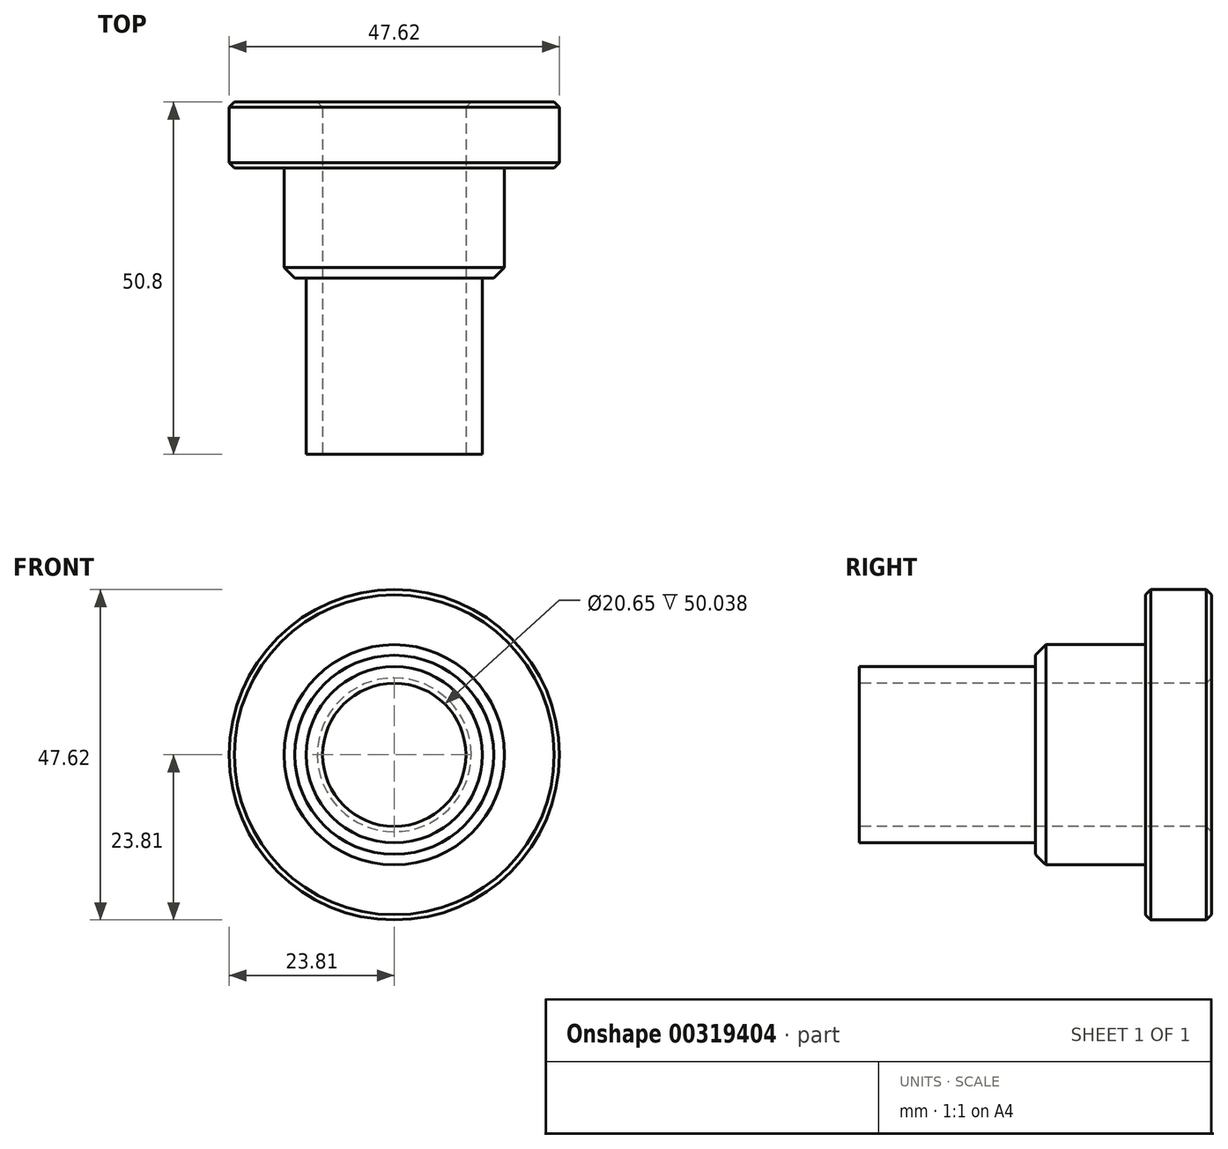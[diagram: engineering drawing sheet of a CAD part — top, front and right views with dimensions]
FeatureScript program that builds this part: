
annotation { "Feature Type Name" : "Feature", "Feature Type Description" : "" }
export const myFeature = defineFeature(function(context is Context, id is Id, definition is map)
    precondition{}
    {
        {
            var Q0;
            Q0=qCreatedBy(makeId("Front.planeOp"),FACE);
            var sketch = newSketch(context, id + "F0", { "sketchPlane" : qUnion([Q0])});
            skCircle(sketch, "E0", {"center": v(0, 0) * mm, "radius": 23.81 * mm});
            skSolve(sketch);
        }
        {
            var Q0;
            Q0 = qSketchRegion(id + "F0", true);
            extrude(context, id + "F1", {"entities" : qUnion([Q0]), "depth" : 9.52 * mm});
        }
        {
            var Q0;
            Q0=makeQuery(id+"F1.opExtrude","CAP_FACE",FACE,{"disambiguationData":[OSD([sQuery(id+"F0.wireOp",EDGE,"E0")])],"isStart":false});
            var sketch = newSketch(context, id + "F2", { "sketchPlane" : qUnion([Q0])});
            skCircle(sketch, "E1", {"center": v(0, 0) * mm, "radius": 15.88 * mm});
            skSolve(sketch);
        }
        {
            var Q0;
            Q0 = qSketchRegion(id + "F2", true);
            extrude(context, id + "F3", {"entities" : qUnion([Q0]), "operationType" : NewBodyOperationType.ADD, "depth" : 15.88 * mm});
        }
        {
            var Q0;
            Q0=makeQuery(id+"F3.opExtrude","CAP_FACE",FACE,{"disambiguationData":[OSD([sQuery(id+"F2.wireOp",EDGE,"E1")])],"isStart":false});
            var sketch = newSketch(context, id + "F4", { "sketchPlane" : qUnion([Q0])});
            skCircle(sketch, "E2", {"center": v(0, 0) * mm, "radius": 12.7 * mm});
            skSolve(sketch);
        }
        {
            var Q0;
            Q0 = qSketchRegion(id + "F4", true);
            extrude(context, id + "F5", {"entities" : qUnion([Q0]), "operationType" : NewBodyOperationType.ADD, "depth" : 25.4 * mm});
        }
        {
            var Q0;
            Q0=makeQuery(id+"F5.opExtrude","CAP_FACE",FACE,{"disambiguationData":[OSD([sQuery(id+"F4.wireOp",EDGE,"E2")])],"isStart":false});
            var sketch = newSketch(context, id + "F6", { "sketchPlane" : qUnion([Q0])});
            skCircle(sketch, "E3", {"center": v(0, 0) * mm, "radius": 10.33 * mm});
            skSolve(sketch);
        }
        {
            var Q0;
            Q0 = qSketchRegion(id + "F6", true);
            extrude(context, id + "F7", {"entities" : qUnion([Q0]), "operationType" : NewBodyOperationType.REMOVE, "endBound" : BoundingType.THROUGH_ALL, "oppositeDirection" : true, "depth" : 25.4 * mm});
        }
        {
            var Q0;
            Q0=makeQuery(id+"F3.opExtrude","CAP_EDGE",EDGE,{"disambiguationData":[OSD([sQuery(id+"F2.wireOp",EDGE,"E1")])],"isStart":false});
            chamfer(context, id + "F8", {"entities" : qUnion([Q0]), "width" : 1.52 * mm, "tangentPropagation" : true});
        }
        {
            var Q0;
            Q0=makeQuery(id+"F1.opExtrude","CAP_EDGE",EDGE,{"disambiguationData":[OSD([sQuery(id+"F0.wireOp",EDGE,"E0")])],"isStart":false});
            var Q1;
            Q1=makeQuery(id+"F1.opExtrude","CAP_EDGE",EDGE,{"disambiguationData":[OSD([sQuery(id+"F0.wireOp",EDGE,"E0")])],"isStart":true});
            var Q2;
            Q2=makeQuery(id+"F7.boolean.opBoolean","INTERSECT",EDGE,{"derivedFrom":[makeQuery(id+"F1.opExtrude","CAP_FACE",FACE,{"disambiguationData":[OSD([sQuery(id+"F0.wireOp",EDGE,"E0")])],"isStart":true}),makeQuery(id+"F7.opExtrude","SWEPT_FACE",FACE,{"disambiguationData":[OSD([sQuery(id+"F6.wireOp",EDGE,"E3")])]})]});
            chamfer(context, id + "F9", {"entities" : qUnion([Q0, Q1, Q2]), "width" : 0.76 * mm, "tangentPropagation" : true});
        }
    });
